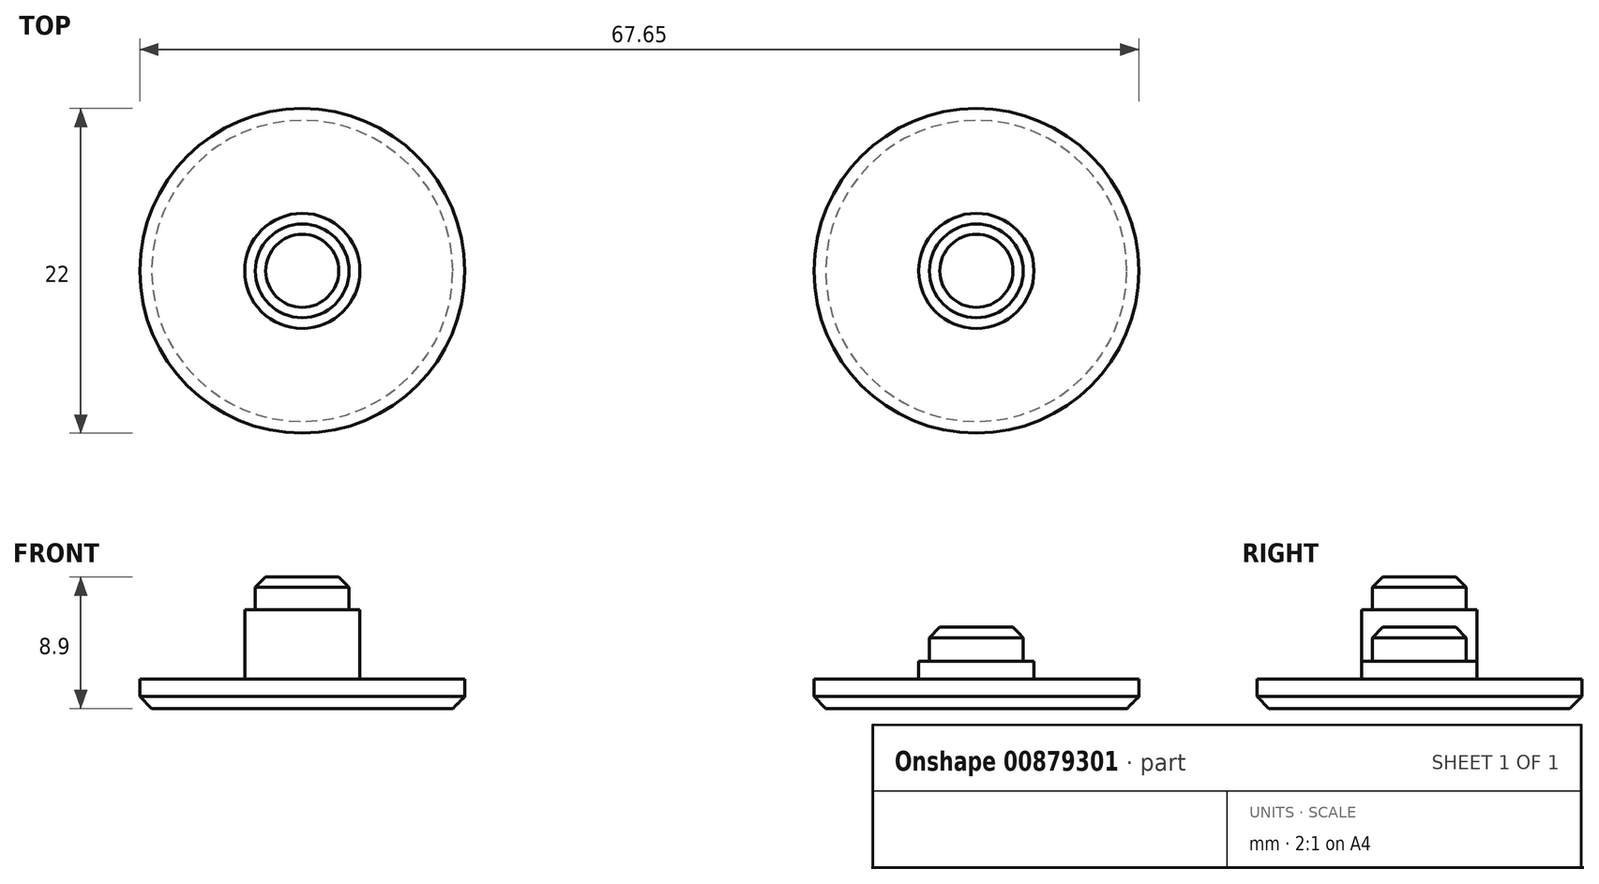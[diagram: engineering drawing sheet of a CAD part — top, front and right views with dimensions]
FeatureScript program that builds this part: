
annotation { "Feature Type Name" : "Feature", "Feature Type Description" : "" }
export const myFeature = defineFeature(function(context is Context, id is Id, definition is map)
    precondition{}
    {
        {
            var Q0;
            Q0=qCreatedBy(makeId("Top.planeOp"),FACE);
            var sketch = newSketch(context, id + "F0", { "sketchPlane" : qUnion([Q0])});
            skCircle(sketch, "E0", {"center": v(0, 0) * mm, "radius": 11 * mm});
            skCircle(sketch, "E1", {"center": v(0, 0) * mm, "radius": 3.9 * mm});
            skCircle(sketch, "E2", {"center": v(0, 0) * mm, "radius": 3.17 * mm});
            skCircle(sketch, "E3", {"center": v(-45.65, 0) * mm, "radius": 11 * mm});
            skCircle(sketch, "E4", {"center": v(-45.65, 0) * mm, "radius": 3.9 * mm});
            skCircle(sketch, "E5", {"center": v(-45.65, 0) * mm, "radius": 3.17 * mm});
            skSolve(sketch);
        }
        {
            var Q0;
            Q0=makeQuery(id+"F0.imprint","IMPRINT",FACE,{"disambiguationData":[TD([[makeQuery(id+"F0.imprint","IMPRINT",EDGE,{"derivedFrom":sQuery(id+"F0.wireOp",EDGE,"E3")}),1.0]])]});
            var Q1;
            Q1=makeQuery(id+"F0.imprint","IMPRINT",FACE,{"disambiguationData":[TD([[makeQuery(id+"F0.imprint","IMPRINT",EDGE,{"derivedFrom":sQuery(id+"F0.wireOp",EDGE,"E5")}),1.0]])]});
            var Q2;
            Q2=makeQuery(id+"F0.imprint","IMPRINT",FACE,{"disambiguationData":[TD([[makeQuery(id+"F0.imprint","IMPRINT",EDGE,{"derivedFrom":sQuery(id+"F0.wireOp",EDGE,"E4")}),1.0]])]});
            var Q3;
            Q3=makeQuery(id+"F0.imprint","IMPRINT",FACE,{"disambiguationData":[TD([[makeQuery(id+"F0.imprint","IMPRINT",EDGE,{"derivedFrom":sQuery(id+"F0.wireOp",EDGE,"E0")}),1.0]])]});
            var Q4;
            Q4=makeQuery(id+"F0.imprint","IMPRINT",FACE,{"disambiguationData":[TD([[makeQuery(id+"F0.imprint","IMPRINT",EDGE,{"derivedFrom":sQuery(id+"F0.wireOp",EDGE,"E1")}),1.0]])]});
            var Q5;
            Q5=makeQuery(id+"F0.imprint","IMPRINT",FACE,{"disambiguationData":[TD([[makeQuery(id+"F0.imprint","IMPRINT",EDGE,{"derivedFrom":sQuery(id+"F0.wireOp",EDGE,"E2")}),1.0]])]});
            extrude(context, id + "F1", {"entities" : qUnion([Q0, Q1, Q2, Q3, Q4, Q5]), "depth" : 2 * mm, "offsetDistance" : 25 * mm});
        }
        {
            var Q0;
            Q0=makeQuery(id+"F0.imprint","IMPRINT",FACE,{"disambiguationData":[TD([[makeQuery(id+"F0.imprint","IMPRINT",EDGE,{"derivedFrom":sQuery(id+"F0.wireOp",EDGE,"E5")}),1.0]])]});
            var Q1;
            Q1=makeQuery(id+"F0.imprint","IMPRINT",FACE,{"disambiguationData":[TD([[makeQuery(id+"F0.imprint","IMPRINT",EDGE,{"derivedFrom":sQuery(id+"F0.wireOp",EDGE,"E4")}),1.0]])]});
            extrude(context, id + "F2", {"entities" : qUnion([Q0, Q1]), "operationType" : NewBodyOperationType.ADD, "depth" : 6.7 * mm, "offsetDistance" : 25 * mm});
        }
        {
            var Q0;
            Q0=makeQuery(id+"F0.imprint","IMPRINT",FACE,{"disambiguationData":[TD([[makeQuery(id+"F0.imprint","IMPRINT",EDGE,{"derivedFrom":sQuery(id+"F0.wireOp",EDGE,"E5")}),1.0]])]});
            extrude(context, id + "F3", {"entities" : qUnion([Q0]), "operationType" : NewBodyOperationType.ADD, "depth" : 8.9 * mm, "offsetDistance" : 25 * mm});
        }
        {
            var Q0;
            Q0=makeQuery(id+"F0.imprint","IMPRINT",FACE,{"disambiguationData":[TD([[makeQuery(id+"F0.imprint","IMPRINT",EDGE,{"derivedFrom":sQuery(id+"F0.wireOp",EDGE,"E2")}),1.0]])]});
            var Q1;
            Q1=makeQuery(id+"F0.imprint","IMPRINT",FACE,{"disambiguationData":[TD([[makeQuery(id+"F0.imprint","IMPRINT",EDGE,{"derivedFrom":sQuery(id+"F0.wireOp",EDGE,"E1")}),1.0]])]});
            extrude(context, id + "F4", {"entities" : qUnion([Q0, Q1]), "operationType" : NewBodyOperationType.ADD, "depth" : 3.2 * mm, "offsetDistance" : 25 * mm});
        }
        {
            var Q0;
            Q0=makeQuery(id+"F0.imprint","IMPRINT",FACE,{"disambiguationData":[TD([[makeQuery(id+"F0.imprint","IMPRINT",EDGE,{"derivedFrom":sQuery(id+"F0.wireOp",EDGE,"E2")}),1.0]])]});
            extrude(context, id + "F5", {"entities" : qUnion([Q0]), "operationType" : NewBodyOperationType.ADD, "depth" : 5.5 * mm, "offsetDistance" : 25 * mm});
        }
        {
            var Q0;
            Q0=makeQuery(id+"F1.opExtrude","CAP_EDGE",EDGE,{"disambiguationData":[OSD([sQuery(id+"F0.wireOp",EDGE,"E3")])],"isStart":true});
            var Q1;
            Q1=makeQuery(id+"F1.opExtrude","CAP_EDGE",EDGE,{"disambiguationData":[OSD([sQuery(id+"F0.wireOp",EDGE,"E0")])],"isStart":true});
            chamfer(context, id + "F6", {"entities" : qUnion([Q0, Q1]), "width" : 0.8 * mm, "tangentPropagation" : true});
        }
        {
            var Q0;
            Q0=makeQuery(id+"F3.opExtrude","CAP_EDGE",EDGE,{"disambiguationData":[OSD([sQuery(id+"F0.wireOp",EDGE,"E5")])],"isStart":false});
            var Q1;
            Q1=makeQuery(id+"F5.opExtrude","CAP_EDGE",EDGE,{"disambiguationData":[OSD([sQuery(id+"F0.wireOp",EDGE,"E2")])],"isStart":false});
            chamfer(context, id + "F7", {"entities" : qUnion([Q0, Q1]), "width" : 0.7 * mm, "tangentPropagation" : true});
        }
    });
